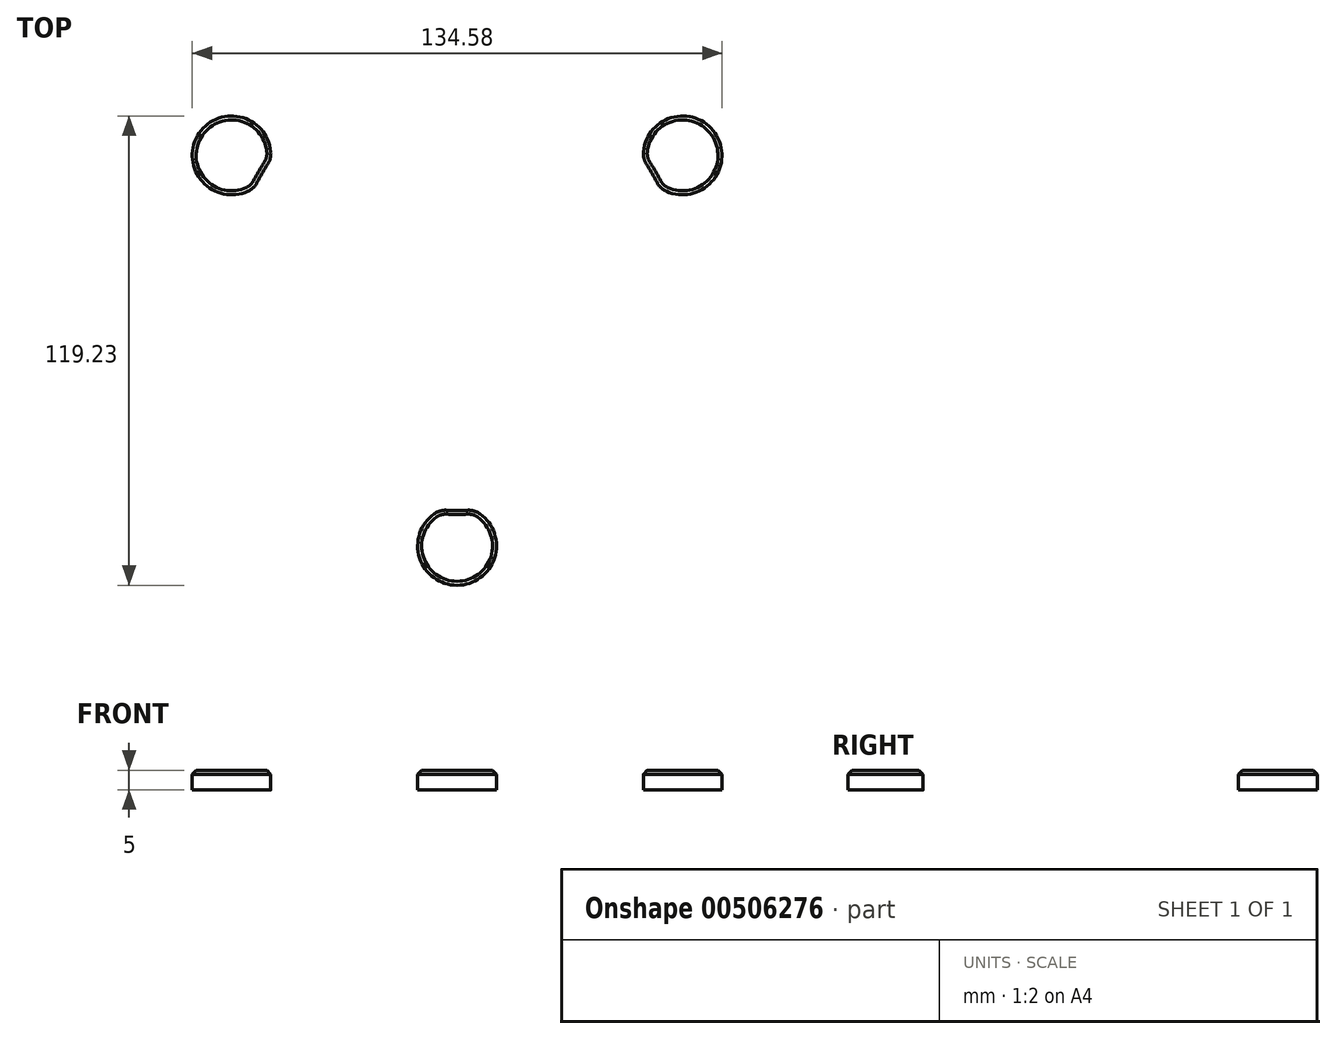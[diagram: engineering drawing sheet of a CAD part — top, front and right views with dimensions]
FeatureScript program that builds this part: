
annotation { "Feature Type Name" : "Feature", "Feature Type Description" : "" }
export const myFeature = defineFeature(function(context is Context, id is Id, definition is map)
    precondition{}
    {
        {
            var Q0;
            Q0=qCreatedBy(makeId("Top.planeOp"),FACE);
            var sketch = newSketch(context, id + "F0", { "sketchPlane" : qUnion([Q0])});
            skCircle(sketch, "E0", {"center": v(0, 0) * mm, "radius": 57.15 * mm});
            skArc(sketch, "E1", {"start": v(-4.05, -57) * mm, "mid": v(0, -76.15) * mm, "end": v(4.05, -57) * mm});
            skArc(sketch, "E2.1.0", {"start": v(51.4, 25) * mm, "mid": v(65.95, 38.07) * mm, "end": v(47.34, 32) * mm});
            skArc(sketch, "E2.1.1", {"start": v(47.34, 32) * mm, "mid": v(-49.5, -28.57) * mm, "end": v(51.4, 25) * mm});
            skArc(sketch, "E2.2.0", {"start": v(-47.34, 32) * mm, "mid": v(-65.95, 38.08) * mm, "end": v(-51.4, 25) * mm});
            skArc(sketch, "E2.2.1", {"start": v(4.05, -57) * mm, "mid": v(49.5, 28.57) * mm, "end": v(-47.34, 32) * mm});
            skArc(sketch, "E3.trimOffspring", {"start": v(-51.4, 25) * mm, "mid": v(-49.5, -28.58) * mm, "end": v(-4.05, -57) * mm});
            skSolve(sketch);
        }
        {
            var Q0;
            {var subQ1=sQuery(id+"F0.wireOp",EDGE,"E0");var subQ6=sQuery(id+"F0.wireOp",EDGE,"E2.1.0");var subQ8=makeQuery(id+"F0.imprint","INTERSECT",VERTEX,{"disambiguationData":[OD(0.0)],"derivedFrom":[subQ1,subQ6]});Q0=makeQuery(id+"F0.imprint","IMPRINT",FACE,{"disambiguationData":[TD([[makeQuery(id+"F0.imprint","IMPRINT",EDGE,{"disambiguationData":[TD([[subQ8,-1.0]])],"derivedFrom":subQ1}),1.0]])]});}
            var Q1;
            {var subQ0=sQuery(id+"F0.wireOp",EDGE,"E2.1.0");Q1=makeQuery(id+"F0.imprint","IMPRINT",FACE,{"disambiguationData":[TD([[makeQuery(id+"F0.imprint","IMPRINT",EDGE,{"derivedFrom":subQ0}),1.0]])]});}
            var Q2;
            {var subQ0=sQuery(id+"F0.wireOp",EDGE,"E2.2.0");Q2=makeQuery(id+"F0.imprint","IMPRINT",FACE,{"disambiguationData":[TD([[makeQuery(id+"F0.imprint","IMPRINT",EDGE,{"derivedFrom":subQ0}),1.0]])]});}
            var Q3;
            {var subQ0=sQuery(id+"F0.wireOp",EDGE,"E1");Q3=makeQuery(id+"F0.imprint","IMPRINT",FACE,{"disambiguationData":[TD([[makeQuery(id+"F0.imprint","IMPRINT",EDGE,{"derivedFrom":subQ0}),1.0]])]});}
            extrude(context, id + "F1", {"entities" : qUnion([Q0, Q1, Q2, Q3]), "depth" : 5 * mm});
        }
        {
            var Q0;
            {var subQ0=sQuery(id+"F0.wireOp",EDGE,"E2.1.0");var subQ1=sQuery(id+"F0.wireOp",EDGE,"E0");Q0=makeQuery(id+"F1.opExtrude","SWEPT_EDGE",EDGE,{"disambiguationData":[OSD([subQ1,subQ0]),TDD([makeQuery(id+"F0.imprint","INTERSECT",VERTEX,{"disambiguationData":[OD(0.0)],"derivedFrom":[subQ1,subQ0]})])]});}
            var Q1;
            {var subQ0=sQuery(id+"F0.wireOp",EDGE,"E1");var subQ1=sQuery(id+"F0.wireOp",EDGE,"E0");Q1=makeQuery(id+"F1.opExtrude","SWEPT_EDGE",EDGE,{"disambiguationData":[OSD([subQ1,subQ0]),TDD([makeQuery(id+"F0.imprint","INTERSECT",VERTEX,{"disambiguationData":[OD(1.0)],"derivedFrom":[subQ1,subQ0]})])]});}
            var Q2;
            {var subQ0=sQuery(id+"F0.wireOp",EDGE,"E2.1.0");var subQ1=sQuery(id+"F0.wireOp",EDGE,"E0");Q2=makeQuery(id+"F1.opExtrude","SWEPT_EDGE",EDGE,{"disambiguationData":[OSD([subQ1,subQ0]),TDD([makeQuery(id+"F0.imprint","INTERSECT",VERTEX,{"disambiguationData":[OD(1.0)],"derivedFrom":[subQ1,subQ0]})])]});}
            var Q3;
            {var subQ0=sQuery(id+"F0.wireOp",EDGE,"E2.2.0");var subQ1=sQuery(id+"F0.wireOp",EDGE,"E0");Q3=makeQuery(id+"F1.opExtrude","SWEPT_EDGE",EDGE,{"disambiguationData":[OSD([subQ1,subQ0]),TDD([makeQuery(id+"F0.imprint","INTERSECT",VERTEX,{"disambiguationData":[OD(1.0)],"derivedFrom":[subQ1,subQ0]})])]});}
            var Q4;
            {var subQ0=sQuery(id+"F0.wireOp",EDGE,"E2.2.0");var subQ1=sQuery(id+"F0.wireOp",EDGE,"E0");Q4=makeQuery(id+"F1.opExtrude","SWEPT_EDGE",EDGE,{"disambiguationData":[OSD([subQ1,subQ0]),TDD([makeQuery(id+"F0.imprint","INTERSECT",VERTEX,{"disambiguationData":[OD(0.0)],"derivedFrom":[subQ1,subQ0]})])]});}
            var Q5;
            {var subQ0=sQuery(id+"F0.wireOp",EDGE,"E1");var subQ1=sQuery(id+"F0.wireOp",EDGE,"E0");Q5=makeQuery(id+"F1.opExtrude","SWEPT_EDGE",EDGE,{"disambiguationData":[OSD([subQ1,subQ0]),TDD([makeQuery(id+"F0.imprint","INTERSECT",VERTEX,{"disambiguationData":[OD(0.0)],"derivedFrom":[subQ1,subQ0]})])]});}
            fillet(context, id + "F2", {"entities" : qUnion([Q0, Q1, Q2, Q3, Q4, Q5]), "radius" : 5 * mm, "tangentPropagation" : true, "allowEdgeOverflow" : false});
        }
        {
            var Q0;
            Q0=makeQuery(id+"F1.opExtrude","CAP_FACE",FACE,{"disambiguationData":[OSD([sQuery(id+"F0.wireOp",EDGE,"E0"),sQuery(id+"F0.wireOp",EDGE,"E1"),sQuery(id+"F0.wireOp",EDGE,"E2.1.0"),sQuery(id+"F0.wireOp",EDGE,"E2.2.0")])],"isStart":false});
            chamfer(context, id + "F3", {"entities" : qUnion([Q0]), "width" : 1 * mm, "tangentPropagation" : true});
        }
    });
